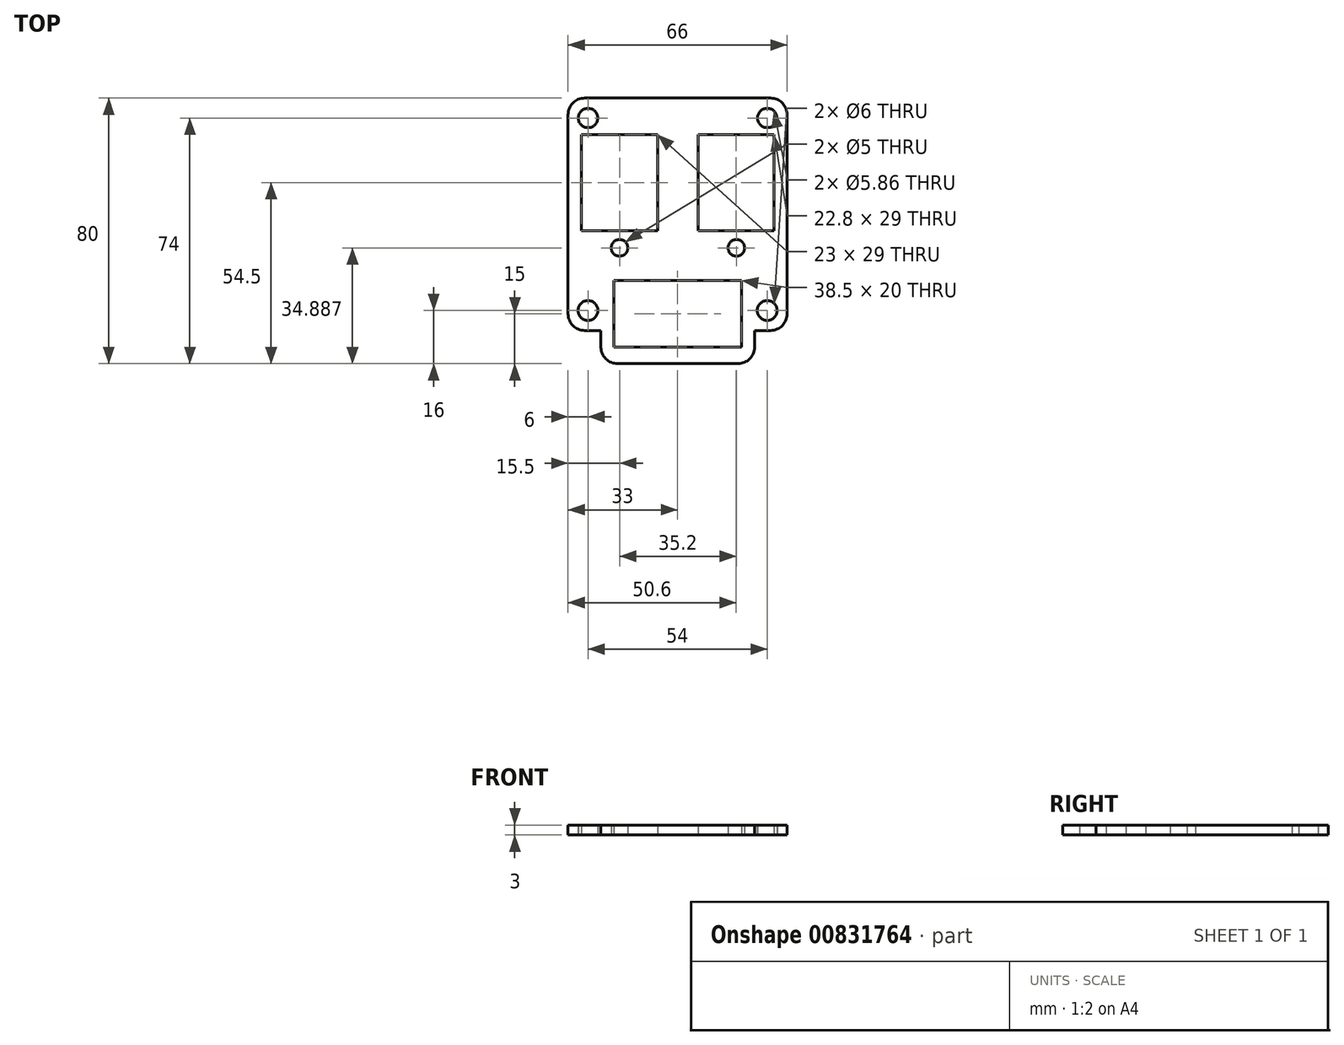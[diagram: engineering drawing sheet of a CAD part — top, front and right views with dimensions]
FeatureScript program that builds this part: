
annotation { "Feature Type Name" : "Feature", "Feature Type Description" : "" }
export const myFeature = defineFeature(function(context is Context, id is Id, definition is map)
    precondition{}
    {
        {
            var Q0;
            Q0=qCreatedBy(makeId("Top.planeOp"),FACE);
            var sketch = newSketch(context, id + "F0", { "sketchPlane" : qUnion([Q0])});
            skLineSegment(sketch, "E0.bottom", {"start": v(4.9, 0) * mm, "end": v(41.2, 0) * mm});
            skLineSegment(sketch, "E0.left", {"start": v(-0.1, 4.9) * mm, "end": v(-0.2, 10) * mm});
            skLineSegment(sketch, "E1.bottom", {"start": v(3.75, 5) * mm, "end": v(42.25, 5) * mm});
            skLineSegment(sketch, "E1.top", {"start": v(3.75, 25) * mm, "end": v(42.25, 25) * mm});
            skLineSegment(sketch, "E1.left", {"start": v(3.75, 5) * mm, "end": v(3.75, 25) * mm});
            skLineSegment(sketch, "E1.right", {"start": v(42.25, 5) * mm, "end": v(42.25, 25) * mm});
            skLineSegment(sketch, "E2", {"start": v(23.1, 5) * mm, "end": v(23.1, 0) * mm, "construction": true});
            skPoint(sketch, "E2.startSnap0", {"position": v(23.1, 0) * mm});
            skPoint(sketch, "E3.endSnap0", {"position": v(3.75, 15) * mm});
            skLineSegment(sketch, "E4.bottom", {"start": v(46.2, 10) * mm, "end": v(51, 10) * mm});
            skLineSegment(sketch, "E4.right", {"start": v(56, 15) * mm, "end": v(56, 15) * mm});
            skCircle(sketch, "E5", {"center": v(50, 16) * mm, "radius": 3 * mm});
            skPoint(sketch, "E5.centerSnap0", {"position": v(50, 21) * mm});
            skLineSegment(sketch, "E6.MirrorCS", {"start": v(-10, 15) * mm, "end": v(-10, 15) * mm});
            skLineSegment(sketch, "E7.MirrorCS", {"start": v(-0.2, 10) * mm, "end": v(-5, 10) * mm});
            skPoint(sketch, "E8.visualSharp", {"position": v(56, 20) * mm});
            skPoint(sketch, "E9.visualSharp", {"position": v(56, 10) * mm});
            skArc(sketch, "E9.filletArc", {"start": v(51, 10) * mm, "mid": v(54.54, 11.46) * mm, "end": v(56, 15) * mm});
            skPoint(sketch, "E10.visualSharp", {"position": v(-10, 20) * mm});
            skPoint(sketch, "E11.visualSharp", {"position": v(-10, 10) * mm});
            skArc(sketch, "E11.filletArc", {"start": v(-10, 15) * mm, "mid": v(-8.54, 11.46) * mm, "end": v(-5, 10) * mm});
            skLineSegment(sketch, "E12.bottom", {"start": v(-6, 40) * mm, "end": v(17, 40) * mm});
            skLineSegment(sketch, "E12.top", {"start": v(-6, 69) * mm, "end": v(17, 69) * mm});
            skLineSegment(sketch, "E12.left", {"start": v(-6, 40) * mm, "end": v(-6, 69) * mm});
            skLineSegment(sketch, "E12.right", {"start": v(17, 40) * mm, "end": v(17, 69) * mm});
            skLineSegment(sketch, "E13", {"start": v(-10, 30) * mm, "end": v(-10, 75) * mm});
            skLineSegment(sketch, "E14", {"start": v(-5, 80) * mm, "end": v(51, 80) * mm});
            skLineSegment(sketch, "E15", {"start": v(56, 75) * mm, "end": v(56, 30) * mm});
            skLineSegment(sketch, "E16.MirrorCS", {"start": v(29.2, 40) * mm, "end": v(29.2, 69) * mm});
            skLineSegment(sketch, "E17.MirrorCS", {"start": v(52.2, 40) * mm, "end": v(29.2, 40) * mm});
            skLineSegment(sketch, "E18.MirrorCS", {"start": v(52, 40) * mm, "end": v(52, 69) * mm});
            skLineSegment(sketch, "E19.MirrorCS", {"start": v(52.2, 69) * mm, "end": v(29.2, 69) * mm});
            skLineSegment(sketch, "E20", {"start": v(-10, 15) * mm, "end": v(-10, 30) * mm});
            skLineSegment(sketch, "E21", {"start": v(56, 15) * mm, "end": v(56, 30) * mm});
            skLineSegment(sketch, "E22", {"start": v(46.2, 5) * mm, "end": v(46.2, 10) * mm});
            skCircle(sketch, "E23", {"center": v(5.5, 34.89) * mm, "radius": 2.5 * mm});
            skPoint(sketch, "E23.centerSnap0", {"position": v(5.5, 40) * mm});
            skCircle(sketch, "E24.MirrorC", {"center": v(40.7, 34.89) * mm, "radius": 2.5 * mm});
            skCircle(sketch, "E25", {"center": v(-4, 74) * mm, "radius": 2.93 * mm});
            skLineSegment(sketch, "E26", {"start": v(23, -7.31) * mm, "end": v(23, 89.93) * mm, "construction": true});
            skCircle(sketch, "E27.MirrorC", {"center": v(50, 74) * mm, "radius": 2.93 * mm});
            skCircle(sketch, "E28.MirrorC", {"center": v(-4, 16) * mm, "radius": 3 * mm});
            skPoint(sketch, "E29.visualSharp", {"position": v(0, 0) * mm});
            skArc(sketch, "E29.filletArc", {"start": v(-0.1, 4.9) * mm, "mid": v(1.4, 1.43) * mm, "end": v(4.9, 0) * mm});
            skPoint(sketch, "E30.visualSharp", {"position": v(46.2, 0) * mm});
            skArc(sketch, "E30.filletArc", {"start": v(41.2, 0) * mm, "mid": v(44.74, 1.46) * mm, "end": v(46.2, 5) * mm});
            skPoint(sketch, "E31.visualSharp", {"position": v(56, 80) * mm});
            skArc(sketch, "E31.filletArc", {"start": v(56, 75) * mm, "mid": v(54.54, 78.54) * mm, "end": v(51, 80) * mm});
            skPoint(sketch, "E32.visualSharp", {"position": v(-10, 80) * mm});
            skArc(sketch, "E32.filletArc", {"start": v(-5, 80) * mm, "mid": v(-8.54, 78.54) * mm, "end": v(-10, 75) * mm});
            skSolve(sketch);
        }
        {
            var Q0;
            Q0=makeQuery(id+"F0.imprint","IMPRINT",FACE,{"disambiguationData":[TD([[makeQuery(id+"F0.imprint","IMPRINT",EDGE,{"derivedFrom":sQuery(id+"F0.wireOp",EDGE,"E0.bottom")}),1.0]])]});
            var Q1;
            {var subQ0=sQuery(id+"F0.wireOp",EDGE,"a72ae289-6ca5-4f3d-ad97-ee05ec2fb1310.MirrorCS");Q1=makeQuery(id+"F0.imprint","IMPRINT",FACE,{"disambiguationData":[TD([[makeQuery(id+"F0.imprint","IMPRINT",EDGE,{"derivedFrom":subQ0}),1.0]])]});}
            var Q2;
            Q2=makeQuery(id+"F0.imprint","IMPRINT",FACE,{"disambiguationData":[TD([[makeQuery(id+"F0.imprint","IMPRINT",EDGE,{"derivedFrom":sQuery(id+"F0.wireOp",EDGE,"E4.bottom")}),1.0]])]});
            extrude(context, id + "F1", {"entities" : qUnion([Q0, Q1, Q2]), "depth" : 3 * mm, "offsetDistance" : 25 * mm});
        }
    });
